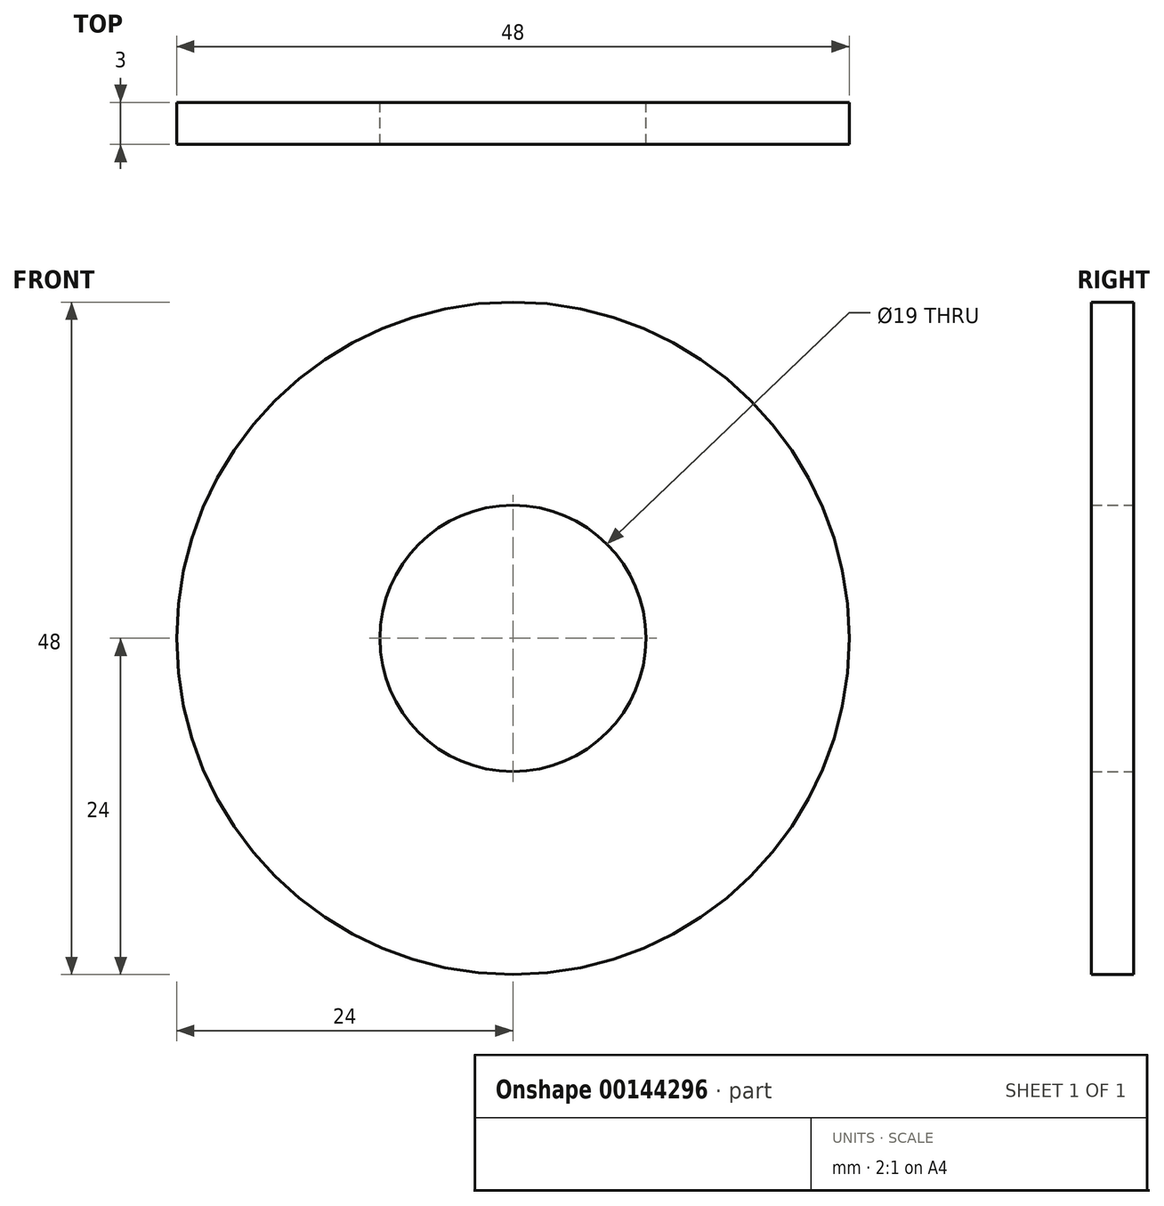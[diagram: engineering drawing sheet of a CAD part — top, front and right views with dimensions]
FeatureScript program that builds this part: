
annotation { "Feature Type Name" : "Feature", "Feature Type Description" : "" }
export const myFeature = defineFeature(function(context is Context, id is Id, definition is map)
    precondition{}
    {
        {
            var Q0;
            Q0=qCreatedBy(makeId("Front.planeOp"),FACE);
            var sketch = newSketch(context, id + "F0", { "sketchPlane" : qUnion([Q0])});
            skCircle(sketch, "E0", {"center": v(0, 0) * mm, "radius": 24 * mm});
            skCircle(sketch, "E1", {"center": v(0, 0) * mm, "radius": 9.5 * mm});
            skSolve(sketch);
        }
        {
            var Q0;
            Q0=makeQuery(id+"F0.imprint","IMPRINT",FACE,{"disambiguationData":[TD([[makeQuery(id+"F0.imprint","IMPRINT",EDGE,{"derivedFrom":sQuery(id+"F0.wireOp",EDGE,"E0")}),1.0]])]});
            extrude(context, id + "F1", {"entities" : qUnion([Q0]), "depth" : 3 * mm});
        }
    });
